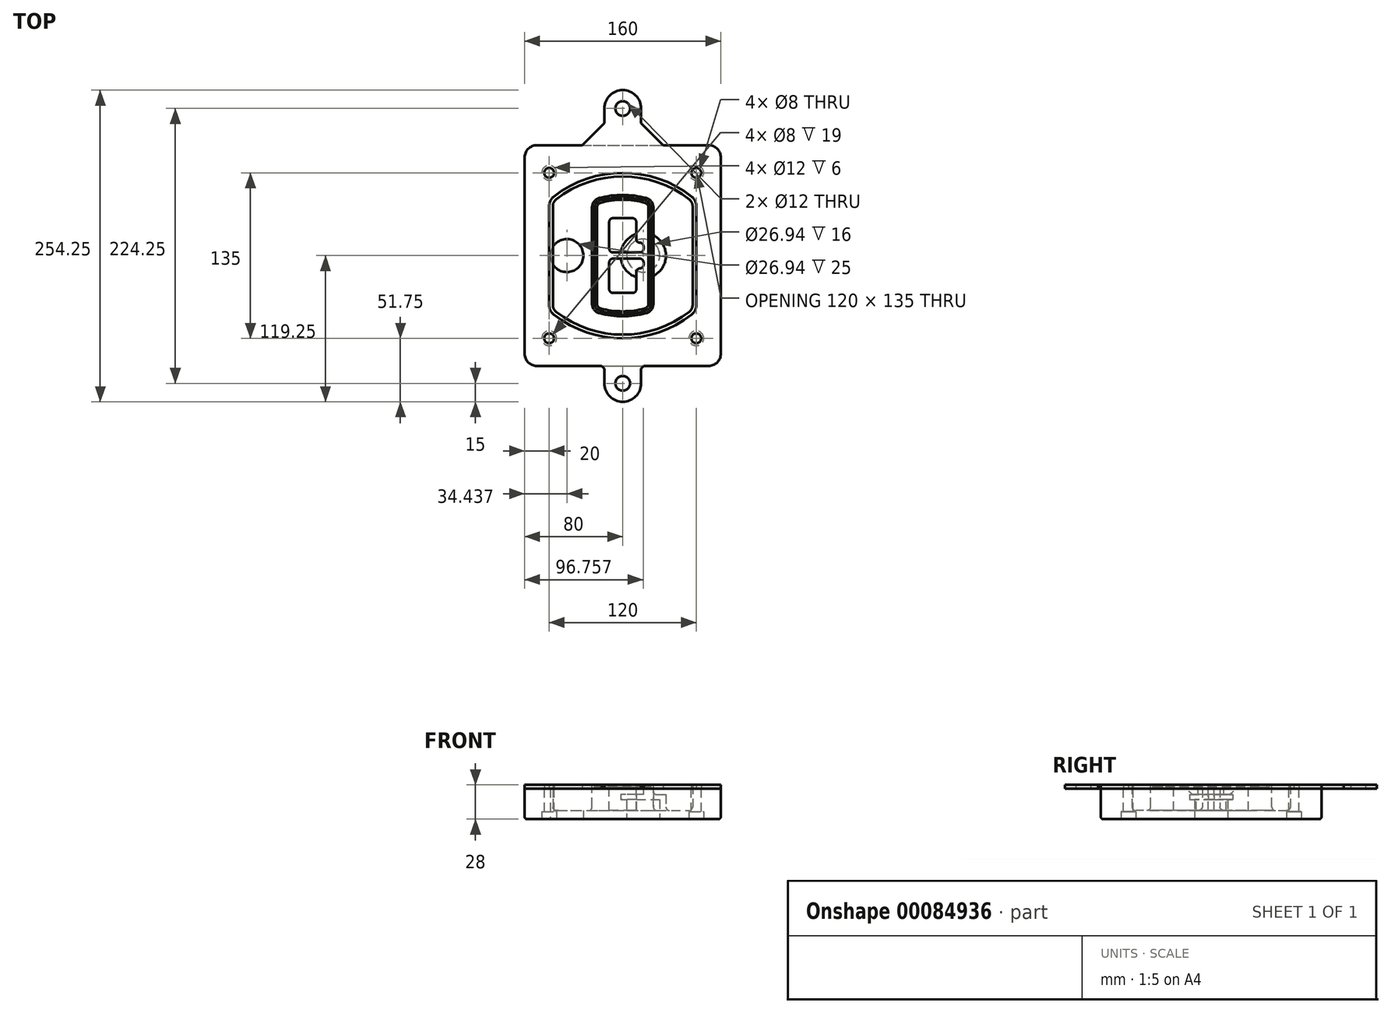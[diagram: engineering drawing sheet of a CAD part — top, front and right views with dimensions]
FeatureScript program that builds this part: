
annotation { "Feature Type Name" : "Feature", "Feature Type Description" : "" }
export const myFeature = defineFeature(function(context is Context, id is Id, definition is map)
    precondition{}
    {
        {
            var Q0;
            Q0=qCreatedBy(makeId("Top.planeOp"),FACE);
            var sketch = newSketch(context, id + "F0", { "sketchPlane" : qUnion([Q0])});
            skPoint(sketch, "E0.rect.middle", {"position": v(0, 0) * mm});
            skLineSegment(sketch, "E1.bottom", {"start": v(-70, -90) * mm, "end": v(70, -90) * mm});
            skLineSegment(sketch, "E1.top", {"start": v(-70, 90) * mm, "end": v(70, 90) * mm});
            skLineSegment(sketch, "E1.left", {"start": v(-80, -80) * mm, "end": v(-80, 80) * mm});
            skLineSegment(sketch, "E1.right", {"start": v(80, -80) * mm, "end": v(80, 80) * mm});
            skLineSegment(sketch, "E2", {"start": v(-80, 90) * mm, "end": v(80, -90) * mm, "construction": true});
            skLineSegment(sketch, "E3", {"start": v(80, 90) * mm, "end": v(-80, -90) * mm, "construction": true});
            skCircle(sketch, "E4", {"center": v(-60, 67.5) * mm, "radius": 4 * mm});
            skCircle(sketch, "E5", {"center": v(60, 67.5) * mm, "radius": 4 * mm});
            skCircle(sketch, "E6", {"center": v(60, -67.5) * mm, "radius": 4 * mm});
            skCircle(sketch, "E7", {"center": v(-60, -67.5) * mm, "radius": 4 * mm});
            skLineSegment(sketch, "E8", {"start": v(-60, 67.5) * mm, "end": v(60, 67.5) * mm, "construction": true});
            skLineSegment(sketch, "E9", {"start": v(60, 67.5) * mm, "end": v(60, -67.5) * mm, "construction": true});
            skLineSegment(sketch, "E10", {"start": v(60, -67.5) * mm, "end": v(-60, -67.5) * mm, "construction": true});
            skLineSegment(sketch, "E11", {"start": v(-60, -67.5) * mm, "end": v(-60, 67.5) * mm, "construction": true});
            skLineSegment(sketch, "E12", {"start": v(-60, 40.3) * mm, "end": v(-60, -40.3) * mm});
            skLineSegment(sketch, "E13", {"start": v(60, 40.3) * mm, "end": v(60, -40.3) * mm});
            skArc(sketch, "E14", {"start": v(56.15, 48.18) * mm, "mid": v(0, 67.5) * mm, "end": v(-56.15, 48.18) * mm});
            skArc(sketch, "E15", {"start": v(-56.15, -48.18) * mm, "mid": v(0, -67.5) * mm, "end": v(56.15, -48.18) * mm});
            skLineSegment(sketch, "E16", {"start": v(-60, 0) * mm, "end": v(60, 0) * mm, "construction": true});
            skPoint(sketch, "E17.visualSharp", {"position": v(-60, -45) * mm});
            skArc(sketch, "E17.filletArc", {"start": v(-60, -40.3) * mm, "mid": v(-58.99, -44.68) * mm, "end": v(-56.15, -48.18) * mm});
            skPoint(sketch, "E18.visualSharp", {"position": v(-60, 45) * mm});
            skArc(sketch, "E18.filletArc", {"start": v(-56.15, 48.18) * mm, "mid": v(-58.99, 44.68) * mm, "end": v(-60, 40.3) * mm});
            skPoint(sketch, "E19.visualSharp", {"position": v(60, 45) * mm});
            skArc(sketch, "E19.filletArc", {"start": v(60, 40.3) * mm, "mid": v(58.99, 44.68) * mm, "end": v(56.15, 48.18) * mm});
            skPoint(sketch, "E20.visualSharp", {"position": v(60, -45) * mm});
            skArc(sketch, "E20.filletArc", {"start": v(56.15, -48.18) * mm, "mid": v(58.99, -44.68) * mm, "end": v(60, -40.3) * mm});
            skPoint(sketch, "E21.visualSharp", {"position": v(-80, 90) * mm});
            skArc(sketch, "E21.filletArc", {"start": v(-70, 90) * mm, "mid": v(-77.07, 87.07) * mm, "end": v(-80, 80) * mm});
            skPoint(sketch, "E22.visualSharp", {"position": v(80, 90) * mm});
            skArc(sketch, "E22.filletArc", {"start": v(80, 80) * mm, "mid": v(77.07, 87.07) * mm, "end": v(70, 90) * mm});
            skPoint(sketch, "E23.visualSharp", {"position": v(80, -90) * mm});
            skArc(sketch, "E23.filletArc", {"start": v(70, -90) * mm, "mid": v(77.07, -87.07) * mm, "end": v(80, -80) * mm});
            skPoint(sketch, "E24.visualSharp", {"position": v(-80, -90) * mm});
            skArc(sketch, "E24.filletArc", {"start": v(-80, -80) * mm, "mid": v(-77.07, -87.07) * mm, "end": v(-70, -90) * mm});
            skArc(sketch, "E25.0", {"start": v(57, 40.3) * mm, "mid": v(56.3, 43.36) * mm, "end": v(54.3, 45.81) * mm});
            skLineSegment(sketch, "E25.1", {"start": v(57, 40.3) * mm, "end": v(57, -40.3) * mm});
            skArc(sketch, "E25.2", {"start": v(54.3, -45.81) * mm, "mid": v(56.3, -43.36) * mm, "end": v(57, -40.3) * mm});
            skArc(sketch, "E25.3", {"start": v(-54.3, -45.81) * mm, "mid": v(0, -64.5) * mm, "end": v(54.3, -45.81) * mm});
            skArc(sketch, "E25.4", {"start": v(-57, -40.3) * mm, "mid": v(-56.3, -43.36) * mm, "end": v(-54.3, -45.81) * mm});
            skArc(sketch, "E25.5", {"start": v(54.3, 45.81) * mm, "mid": v(0, 64.5) * mm, "end": v(-54.3, 45.81) * mm});
            skLineSegment(sketch, "E25.6", {"start": v(-57, 40.3) * mm, "end": v(-57, -40.3) * mm});
            skArc(sketch, "E25.7", {"start": v(-54.3, 45.81) * mm, "mid": v(-56.3, 43.36) * mm, "end": v(-57, 40.3) * mm});
            skArc(sketch, "E26.0", {"start": v(-58.62, 51.33) * mm, "mid": v(-62.58, 46.43) * mm, "end": v(-64, 40.3) * mm});
            skArc(sketch, "E26.1", {"start": v(58.62, 51.33) * mm, "mid": v(0, 71.5) * mm, "end": v(-58.62, 51.33) * mm});
            skArc(sketch, "E26.2", {"start": v(64, 40.3) * mm, "mid": v(62.58, 46.43) * mm, "end": v(58.62, 51.33) * mm});
            skLineSegment(sketch, "E26.3", {"start": v(64, 40.3) * mm, "end": v(64, -40.3) * mm});
            skArc(sketch, "E26.4", {"start": v(58.62, -51.33) * mm, "mid": v(62.58, -46.43) * mm, "end": v(64, -40.3) * mm});
            skLineSegment(sketch, "E26.5", {"start": v(-64, 40.3) * mm, "end": v(-64, -40.3) * mm});
            skArc(sketch, "E26.6", {"start": v(-58.62, -51.33) * mm, "mid": v(0, -71.5) * mm, "end": v(58.62, -51.33) * mm});
            skArc(sketch, "E26.7", {"start": v(-64, -40.3) * mm, "mid": v(-62.58, -46.43) * mm, "end": v(-58.62, -51.33) * mm});
            skSolve(sketch);
        }
        {
            var Q0;
            Q0=makeQuery(id+"F0.imprint","IMPRINT",FACE,{"disambiguationData":[TD([[makeQuery(id+"F0.imprint","IMPRINT",EDGE,{"derivedFrom":sQuery(id+"F0.wireOp",EDGE,"E1.bottom")}),1.0]])]});
            var Q1;
            Q1=makeQuery(id+"F0.imprint","IMPRINT",FACE,{"disambiguationData":[TD([[makeQuery(id+"F0.imprint","IMPRINT",EDGE,{"derivedFrom":sQuery(id+"F0.wireOp",EDGE,"E12")}),1.0]])]});
            var Q2;
            Q2=makeQuery(id+"F0.imprint","IMPRINT",FACE,{"disambiguationData":[TD([[makeQuery(id+"F0.imprint","IMPRINT",EDGE,{"derivedFrom":sQuery(id+"F0.wireOp",EDGE,"E25.0")}),1.0]])]});
            var Q3;
            Q3=makeQuery(id+"F0.imprint","IMPRINT",FACE,{"disambiguationData":[TD([[makeQuery(id+"F0.imprint","IMPRINT",EDGE,{"derivedFrom":sQuery(id+"F0.wireOp",EDGE,"E12")}),-1.0]])]});
            extrude(context, id + "F1", {"entities" : qUnion([Q0, Q1, Q2, Q3]), "oppositeDirection" : true, "depth" : 25 * mm});
        }
        {
            var Q0;
            Q0=makeQuery(id+"F0.imprint","IMPRINT",FACE,{"disambiguationData":[TD([[makeQuery(id+"F0.imprint","IMPRINT",EDGE,{"derivedFrom":sQuery(id+"F0.wireOp",EDGE,"E12")}),1.0]])]});
            extrude(context, id + "F2", {"entities" : qUnion([Q0]), "operationType" : NewBodyOperationType.ADD, "depth" : 3 * mm});
        }
        {
            var Q0;
            Q0=makeQuery(id+"F0.imprint","IMPRINT",FACE,{"disambiguationData":[TD([[makeQuery(id+"F0.imprint","IMPRINT",EDGE,{"derivedFrom":sQuery(id+"F0.wireOp",EDGE,"E25.0")}),1.0]])]});
            extrude(context, id + "F3", {"entities" : qUnion([Q0]), "operationType" : NewBodyOperationType.REMOVE, "oppositeDirection" : true, "depth" : 18 * mm});
        }
        {
            var Q0;
            Q0=makeQuery(id+"F2.opExtrude","CAP_FACE",FACE,{"disambiguationData":[OSD([sQuery(id+"F0.wireOp",EDGE,"E12"),sQuery(id+"F0.wireOp",EDGE,"E13"),sQuery(id+"F0.wireOp",EDGE,"E14"),sQuery(id+"F0.wireOp",EDGE,"E15"),sQuery(id+"F0.wireOp",EDGE,"E17.filletArc"),sQuery(id+"F0.wireOp",EDGE,"E18.filletArc"),sQuery(id+"F0.wireOp",EDGE,"E19.filletArc"),sQuery(id+"F0.wireOp",EDGE,"E20.filletArc"),sQuery(id+"F0.wireOp",EDGE,"E25.0"),sQuery(id+"F0.wireOp",EDGE,"E25.1"),sQuery(id+"F0.wireOp",EDGE,"E25.2"),sQuery(id+"F0.wireOp",EDGE,"E25.3"),sQuery(id+"F0.wireOp",EDGE,"E25.4"),sQuery(id+"F0.wireOp",EDGE,"E25.5"),sQuery(id+"F0.wireOp",EDGE,"E25.6"),sQuery(id+"F0.wireOp",EDGE,"E25.7")])],"isStart":false});
            var sketch = newSketch(context, id + "F4", { "sketchPlane" : qUnion([Q0])});
            skArc(sketch, "E27.0", {"start": v(-19.08, -46.97) * mm, "mid": v(0, -49.5) * mm, "end": v(19.08, -46.97) * mm});
            skArc(sketch, "E28.0", {"start": v(19.08, 46.97) * mm, "mid": v(0, 49.5) * mm, "end": v(-19.08, 46.97) * mm});
            skLineSegment(sketch, "E29", {"start": v(-25, 39.25) * mm, "end": v(-25, -39.25) * mm});
            skLineSegment(sketch, "E30", {"start": v(25, 39.25) * mm, "end": v(25, -39.25) * mm});
            skLineSegment(sketch, "E31", {"start": v(-25, 45.1) * mm, "end": v(25, 45.1) * mm, "construction": true});
            skLineSegment(sketch, "E32", {"start": v(-25, -45.1) * mm, "end": v(25, -45.1) * mm, "construction": true});
            skPoint(sketch, "E33.visualSharp", {"position": v(-25, 45.1) * mm});
            skArc(sketch, "E33.filletArc", {"start": v(-19.08, 46.97) * mm, "mid": v(-23.35, 44.11) * mm, "end": v(-25, 39.25) * mm});
            skPoint(sketch, "E34.visualSharp", {"position": v(25, 45.1) * mm});
            skArc(sketch, "E34.filletArc", {"start": v(25, 39.25) * mm, "mid": v(23.35, 44.11) * mm, "end": v(19.08, 46.97) * mm});
            skPoint(sketch, "E35.visualSharp", {"position": v(25, -45.1) * mm});
            skArc(sketch, "E35.filletArc", {"start": v(19.08, -46.97) * mm, "mid": v(23.35, -44.11) * mm, "end": v(25, -39.25) * mm});
            skPoint(sketch, "E36.visualSharp", {"position": v(-25, -45.1) * mm});
            skArc(sketch, "E36.filletArc", {"start": v(-25, -39.25) * mm, "mid": v(-23.35, -44.11) * mm, "end": v(-19.08, -46.97) * mm});
            skArc(sketch, "E37.0", {"start": v(54.3, 45.81) * mm, "mid": v(0, 64.5) * mm, "end": v(-54.3, 45.81) * mm});
            skArc(sketch, "E37.1", {"start": v(-54.3, 45.81) * mm, "mid": v(-56.3, 43.36) * mm, "end": v(-57, 40.3) * mm});
            skLineSegment(sketch, "E37.2", {"start": v(-57, 40.3) * mm, "end": v(-57, -40.3) * mm});
            skArc(sketch, "E37.3", {"start": v(-57, -40.3) * mm, "mid": v(-56.3, -43.36) * mm, "end": v(-54.3, -45.81) * mm});
            skArc(sketch, "E37.4", {"start": v(-54.3, -45.81) * mm, "mid": v(0, -64.5) * mm, "end": v(54.3, -45.81) * mm});
            skArc(sketch, "E37.5", {"start": v(54.3, -45.81) * mm, "mid": v(56.3, -43.36) * mm, "end": v(57, -40.3) * mm});
            skLineSegment(sketch, "E37.6", {"start": v(57, 40.3) * mm, "end": v(57, -40.3) * mm});
            skArc(sketch, "E37.7", {"start": v(57, 40.3) * mm, "mid": v(56.3, 43.36) * mm, "end": v(54.3, 45.81) * mm});
            skLineSegment(sketch, "E38.0", {"start": v(23, 39.25) * mm, "end": v(23, -39.25) * mm});
            skArc(sketch, "E38.1", {"start": v(18.56, -45.04) * mm, "mid": v(21.76, -42.9) * mm, "end": v(23, -39.25) * mm});
            skArc(sketch, "E38.2", {"start": v(-18.56, -45.04) * mm, "mid": v(0, -47.5) * mm, "end": v(18.56, -45.04) * mm});
            skArc(sketch, "E38.3", {"start": v(-23, -39.25) * mm, "mid": v(-21.76, -42.9) * mm, "end": v(-18.56, -45.04) * mm});
            skLineSegment(sketch, "E38.4", {"start": v(-23, 39.25) * mm, "end": v(-23, -39.25) * mm});
            skArc(sketch, "E38.5", {"start": v(23, 39.25) * mm, "mid": v(21.76, 42.9) * mm, "end": v(18.56, 45.04) * mm});
            skArc(sketch, "E38.6", {"start": v(-18.56, 45.04) * mm, "mid": v(-21.76, 42.9) * mm, "end": v(-23, 39.25) * mm});
            skArc(sketch, "E38.7", {"start": v(18.56, 45.04) * mm, "mid": v(0, 47.5) * mm, "end": v(-18.56, 45.04) * mm});
            skArc(sketch, "E39.0", {"start": v(21, 39.25) * mm, "mid": v(20.18, 41.68) * mm, "end": v(18.04, 43.1) * mm});
            skLineSegment(sketch, "E39.1", {"start": v(21, 39.25) * mm, "end": v(21, -39.25) * mm});
            skArc(sketch, "E39.2", {"start": v(18.04, -43.1) * mm, "mid": v(20.18, -41.68) * mm, "end": v(21, -39.25) * mm});
            skArc(sketch, "E39.3", {"start": v(-18.04, -43.1) * mm, "mid": v(0, -45.5) * mm, "end": v(18.04, -43.1) * mm});
            skArc(sketch, "E39.4", {"start": v(-21, -39.25) * mm, "mid": v(-20.18, -41.68) * mm, "end": v(-18.04, -43.1) * mm});
            skArc(sketch, "E39.5", {"start": v(18.04, 43.1) * mm, "mid": v(0, 45.5) * mm, "end": v(-18.04, 43.1) * mm});
            skLineSegment(sketch, "E39.6", {"start": v(-21, 39.25) * mm, "end": v(-21, -39.25) * mm});
            skArc(sketch, "E39.7", {"start": v(-18.04, 43.1) * mm, "mid": v(-20.18, 41.68) * mm, "end": v(-21, 39.25) * mm});
            skLineSegment(sketch, "E40", {"start": v(-25, 0) * mm, "end": v(25, 0) * mm, "construction": true});
            skLineSegment(sketch, "E41", {"start": v(-11, 5.5) * mm, "end": v(-11, 27.5) * mm});
            skLineSegment(sketch, "E42", {"start": v(-8, 30.5) * mm, "end": v(8, 30.5) * mm});
            skLineSegment(sketch, "E43", {"start": v(11, 27.5) * mm, "end": v(11, 13.5) * mm});
            skLineSegment(sketch, "E44", {"start": v(14, 10.5) * mm, "end": v(14, 10.5) * mm});
            skLineSegment(sketch, "E45", {"start": v(17, 7.5) * mm, "end": v(17, 5.5) * mm});
            skLineSegment(sketch, "E46", {"start": v(14, 2.5) * mm, "end": v(-8, 2.5) * mm});
            skPoint(sketch, "E47.visualSharp", {"position": v(-11, 30.5) * mm});
            skArc(sketch, "E47.filletArc", {"start": v(-8, 30.5) * mm, "mid": v(-10.12, 29.62) * mm, "end": v(-11, 27.5) * mm});
            skPoint(sketch, "E48.visualSharp", {"position": v(11, 30.5) * mm});
            skArc(sketch, "E48.filletArc", {"start": v(11, 27.5) * mm, "mid": v(10.12, 29.62) * mm, "end": v(8, 30.5) * mm});
            skPoint(sketch, "E49.visualSharp", {"position": v(11, 10.5) * mm});
            skArc(sketch, "E49.filletArc", {"start": v(11, 13.5) * mm, "mid": v(11.88, 11.38) * mm, "end": v(14, 10.5) * mm});
            skPoint(sketch, "E50.visualSharp", {"position": v(17, 10.5) * mm});
            skArc(sketch, "E50.filletArc", {"start": v(17, 7.5) * mm, "mid": v(16.12, 9.62) * mm, "end": v(14, 10.5) * mm});
            skPoint(sketch, "E51.visualSharp", {"position": v(17, 2.5) * mm});
            skArc(sketch, "E51.filletArc", {"start": v(14, 2.5) * mm, "mid": v(16.12, 3.38) * mm, "end": v(17, 5.5) * mm});
            skPoint(sketch, "E52.visualSharp", {"position": v(-11, 2.5) * mm});
            skArc(sketch, "E52.filletArc", {"start": v(-11, 5.5) * mm, "mid": v(-10.12, 3.38) * mm, "end": v(-8, 2.5) * mm});
            skLineSegment(sketch, "E53.0.MirrorCS", {"start": v(14, -2.5) * mm, "end": v(-8, -2.5) * mm});
            skArc(sketch, "E54.0.MirrorCS", {"start": v(-11, -5.5) * mm, "mid": v(-10.12, -3.38) * mm, "end": v(-8, -2.5) * mm});
            skLineSegment(sketch, "E55.0.MirrorCS", {"start": v(-11, -5.5) * mm, "end": v(-11, -27.5) * mm});
            skArc(sketch, "E56.0.MirrorCS", {"start": v(-8, -30.5) * mm, "mid": v(-10.12, -29.62) * mm, "end": v(-11, -27.5) * mm});
            skLineSegment(sketch, "E57.0.MirrorCS", {"start": v(-8, -30.5) * mm, "end": v(8, -30.5) * mm});
            skArc(sketch, "E58.0.MirrorCS", {"start": v(11, -27.5) * mm, "mid": v(10.12, -29.62) * mm, "end": v(8, -30.5) * mm});
            skLineSegment(sketch, "E59.0.MirrorCS", {"start": v(11, -27.5) * mm, "end": v(11, -13.5) * mm});
            skArc(sketch, "E60.0.MirrorCS", {"start": v(11, -13.5) * mm, "mid": v(11.88, -11.38) * mm, "end": v(14, -10.5) * mm});
            skArc(sketch, "E61.0.MirrorCS", {"start": v(17, -7.5) * mm, "mid": v(16.12, -9.62) * mm, "end": v(14, -10.5) * mm});
            skLineSegment(sketch, "E62.0.MirrorCS", {"start": v(17, -7.5) * mm, "end": v(17, -5.5) * mm});
            skArc(sketch, "E63.0.MirrorCS", {"start": v(14, -2.5) * mm, "mid": v(16.12, -3.38) * mm, "end": v(17, -5.5) * mm});
            skSolve(sketch);
        }
        {
            var Q0;
            Q0=makeQuery(id+"F4.imprint","IMPRINT",FACE,{"disambiguationData":[TD([[makeQuery(id+"F4.imprint","IMPRINT",EDGE,{"derivedFrom":sQuery(id+"F4.wireOp",EDGE,"E27.0")}),1.0]])]});
            var Q1;
            Q1=makeQuery(id+"F4.imprint","IMPRINT",FACE,{"disambiguationData":[TD([[makeQuery(id+"F4.imprint","IMPRINT",EDGE,{"derivedFrom":sQuery(id+"F4.wireOp",EDGE,"E38.0")}),-1.0]])]});
            var Q2;
            Q2=makeQuery(id+"F4.imprint","IMPRINT",FACE,{"disambiguationData":[TD([[makeQuery(id+"F4.imprint","IMPRINT",EDGE,{"derivedFrom":sQuery(id+"F4.wireOp",EDGE,"E39.0")}),1.0]])]});
            extrude(context, id + "F5", {"entities" : qUnion([Q0, Q1, Q2]), "operationType" : NewBodyOperationType.ADD, "endBound" : BoundingType.UP_TO_NEXT, "oppositeDirection" : true, "depth" : 25 * mm});
        }
        {
            var Q0;
            Q0=makeQuery(id+"F4.imprint","IMPRINT",FACE,{"disambiguationData":[TD([[makeQuery(id+"F4.imprint","IMPRINT",EDGE,{"derivedFrom":sQuery(id+"F4.wireOp",EDGE,"E38.0")}),-1.0]])]});
            extrude(context, id + "F6", {"entities" : qUnion([Q0]), "operationType" : NewBodyOperationType.REMOVE, "oppositeDirection" : true, "depth" : 2 * mm});
        }
        {
            var Q0;
            Q0=makeQuery(id+"F1.opExtrude","CAP_FACE",FACE,{"disambiguationData":[OSD([sQuery(id+"F0.wireOp",EDGE,"E1.bottom"),sQuery(id+"F0.wireOp",EDGE,"E1.top"),sQuery(id+"F0.wireOp",EDGE,"E1.left"),sQuery(id+"F0.wireOp",EDGE,"E1.right"),sQuery(id+"F0.wireOp",EDGE,"E4"),sQuery(id+"F0.wireOp",EDGE,"E5"),sQuery(id+"F0.wireOp",EDGE,"E6"),sQuery(id+"F0.wireOp",EDGE,"E7"),sQuery(id+"F0.wireOp",EDGE,"E21.filletArc"),sQuery(id+"F0.wireOp",EDGE,"E22.filletArc"),sQuery(id+"F0.wireOp",EDGE,"E23.filletArc"),sQuery(id+"F0.wireOp",EDGE,"E24.filletArc")])],"isStart":false});
            var sketch = newSketch(context, id + "F7", { "sketchPlane" : qUnion([Q0])});
            skCircle(sketch, "E64", {"center": v(16.76, 0) * mm, "radius": 13.47 * mm});
            skCircle(sketch, "E65", {"center": v(-45.56, 0) * mm, "radius": 13.47 * mm});
            skLineSegment(sketch, "E66", {"start": v(80, 0) * mm, "end": v(-80, 0) * mm});
            skCircle(sketch, "E67", {"center": v(16.76, 0) * mm, "radius": 18.47 * mm});
            skCircle(sketch, "E68", {"center": v(60, -67.5) * mm, "radius": 6 * mm});
            skCircle(sketch, "E69", {"center": v(-60, -67.5) * mm, "radius": 6 * mm});
            skCircle(sketch, "E70", {"center": v(-60, 67.5) * mm, "radius": 6 * mm});
            skCircle(sketch, "E71", {"center": v(60, 67.5) * mm, "radius": 6 * mm});
            skSolve(sketch);
        }
        {
            var Q0;
            {var subQ1=sQuery(id+"F7.wireOp",EDGE,"E66");var subQ4=sQuery(id+"F7.wireOp",EDGE,"E64");var subQ6=makeQuery(id+"F7.imprint","INTERSECT",VERTEX,{"disambiguationData":[OD(0.0)],"derivedFrom":[subQ4,subQ1]});Q0=makeQuery(id+"F7.imprint","IMPRINT",FACE,{"disambiguationData":[TD([[makeQuery(id+"F7.imprint","IMPRINT",EDGE,{"disambiguationData":[TD([[subQ6,-1.0]])],"derivedFrom":subQ4}),-1.0]])]});}
            var Q1;
            {var subQ0=sQuery(id+"F7.wireOp",EDGE,"E66");var subQ1=sQuery(id+"F7.wireOp",EDGE,"E64");var subQ3=makeQuery(id+"F7.imprint","INTERSECT",VERTEX,{"disambiguationData":[OD(0.0)],"derivedFrom":[subQ1,subQ0]});Q1=makeQuery(id+"F7.imprint","IMPRINT",FACE,{"disambiguationData":[TD([[makeQuery(id+"F7.imprint","IMPRINT",EDGE,{"disambiguationData":[TD([[subQ3,-1.0]])],"derivedFrom":subQ1}),1.0]])]});}
            var Q2;
            {var subQ0=sQuery(id+"F7.wireOp",EDGE,"E66");var subQ1=sQuery(id+"F7.wireOp",EDGE,"E64");var subQ3=makeQuery(id+"F7.imprint","INTERSECT",VERTEX,{"disambiguationData":[OD(0.0)],"derivedFrom":[subQ1,subQ0]});Q2=makeQuery(id+"F7.imprint","IMPRINT",FACE,{"disambiguationData":[TD([[makeQuery(id+"F7.imprint","IMPRINT",EDGE,{"disambiguationData":[TD([[subQ3,1.0]])],"derivedFrom":subQ1}),1.0]])]});}
            var Q3;
            {var subQ1=sQuery(id+"F7.wireOp",EDGE,"E66");var subQ4=sQuery(id+"F7.wireOp",EDGE,"E64");var subQ6=makeQuery(id+"F7.imprint","INTERSECT",VERTEX,{"disambiguationData":[OD(0.0)],"derivedFrom":[subQ4,subQ1]});Q3=makeQuery(id+"F7.imprint","IMPRINT",FACE,{"disambiguationData":[TD([[makeQuery(id+"F7.imprint","IMPRINT",EDGE,{"disambiguationData":[TD([[subQ6,1.0]])],"derivedFrom":subQ4}),-1.0]])]});}
            extrude(context, id + "F8", {"entities" : qUnion([Q0, Q1, Q2, Q3]), "operationType" : NewBodyOperationType.ADD, "oppositeDirection" : true, "depth" : 20 * mm});
        }
        {
            var Q0;
            {var subQ0=sQuery(id+"F7.wireOp",EDGE,"E66");var subQ1=sQuery(id+"F7.wireOp",EDGE,"E64");var subQ3=makeQuery(id+"F7.imprint","INTERSECT",VERTEX,{"disambiguationData":[OD(0.0)],"derivedFrom":[subQ1,subQ0]});Q0=makeQuery(id+"F7.imprint","IMPRINT",FACE,{"disambiguationData":[TD([[makeQuery(id+"F7.imprint","IMPRINT",EDGE,{"disambiguationData":[TD([[subQ3,-1.0]])],"derivedFrom":subQ1}),1.0]])]});}
            var Q1;
            {var subQ0=sQuery(id+"F7.wireOp",EDGE,"E66");var subQ1=sQuery(id+"F7.wireOp",EDGE,"E64");var subQ3=makeQuery(id+"F7.imprint","INTERSECT",VERTEX,{"disambiguationData":[OD(0.0)],"derivedFrom":[subQ1,subQ0]});Q1=makeQuery(id+"F7.imprint","IMPRINT",FACE,{"disambiguationData":[TD([[makeQuery(id+"F7.imprint","IMPRINT",EDGE,{"disambiguationData":[TD([[subQ3,1.0]])],"derivedFrom":subQ1}),1.0]])]});}
            extrude(context, id + "F9", {"entities" : qUnion([Q0, Q1]), "operationType" : NewBodyOperationType.REMOVE, "oppositeDirection" : true, "depth" : 16 * mm});
        }
        {
            var Q0;
            {var subQ0=sQuery(id+"F7.wireOp",EDGE,"E66");var subQ1=sQuery(id+"F7.wireOp",EDGE,"E65");var subQ3=makeQuery(id+"F7.imprint","INTERSECT",VERTEX,{"disambiguationData":[OD(0.0)],"derivedFrom":[subQ1,subQ0]});Q0=makeQuery(id+"F7.imprint","IMPRINT",FACE,{"disambiguationData":[TD([[makeQuery(id+"F7.imprint","IMPRINT",EDGE,{"disambiguationData":[TD([[subQ3,-1.0]])],"derivedFrom":subQ1}),1.0]])]});}
            var Q1;
            {var subQ0=sQuery(id+"F7.wireOp",EDGE,"E66");var subQ1=sQuery(id+"F7.wireOp",EDGE,"E65");var subQ3=makeQuery(id+"F7.imprint","INTERSECT",VERTEX,{"disambiguationData":[OD(0.0)],"derivedFrom":[subQ1,subQ0]});Q1=makeQuery(id+"F7.imprint","IMPRINT",FACE,{"disambiguationData":[TD([[makeQuery(id+"F7.imprint","IMPRINT",EDGE,{"disambiguationData":[TD([[subQ3,1.0]])],"derivedFrom":subQ1}),1.0]])]});}
            extrude(context, id + "F10", {"entities" : qUnion([Q0, Q1]), "operationType" : NewBodyOperationType.REMOVE, "oppositeDirection" : true, "depth" : 25 * mm});
        }
        {
            var Q0;
            Q0=makeQuery(id+"F7.imprint","IMPRINT",FACE,{"disambiguationData":[TD([[makeQuery(id+"F7.imprint","IMPRINT",EDGE,{"derivedFrom":sQuery(id+"F7.wireOp",EDGE,"E68")}),1.0]])]});
            var Q1;
            Q1=makeQuery(id+"F7.imprint","IMPRINT",FACE,{"disambiguationData":[TD([[makeQuery(id+"F7.imprint","IMPRINT",EDGE,{"derivedFrom":makeQuery(id+"F1.opExtrude","CAP_EDGE",EDGE,{"disambiguationData":[OSD([sQuery(id+"F0.wireOp",EDGE,"E5")])],"isStart":false})}),-1.0]])]});
            var Q2;
            Q2=makeQuery(id+"F7.imprint","IMPRINT",FACE,{"disambiguationData":[TD([[makeQuery(id+"F7.imprint","IMPRINT",EDGE,{"derivedFrom":sQuery(id+"F7.wireOp",EDGE,"E69")}),1.0]])]});
            var Q3;
            Q3=makeQuery(id+"F7.imprint","IMPRINT",FACE,{"disambiguationData":[TD([[makeQuery(id+"F7.imprint","IMPRINT",EDGE,{"derivedFrom":makeQuery(id+"F1.opExtrude","CAP_EDGE",EDGE,{"disambiguationData":[OSD([sQuery(id+"F0.wireOp",EDGE,"E4")])],"isStart":false})}),-1.0]])]});
            var Q4;
            Q4=makeQuery(id+"F7.imprint","IMPRINT",FACE,{"disambiguationData":[TD([[makeQuery(id+"F7.imprint","IMPRINT",EDGE,{"derivedFrom":sQuery(id+"F7.wireOp",EDGE,"E70")}),1.0]])]});
            var Q5;
            Q5=makeQuery(id+"F7.imprint","IMPRINT",FACE,{"disambiguationData":[TD([[makeQuery(id+"F7.imprint","IMPRINT",EDGE,{"derivedFrom":makeQuery(id+"F1.opExtrude","CAP_EDGE",EDGE,{"disambiguationData":[OSD([sQuery(id+"F0.wireOp",EDGE,"E7")])],"isStart":false})}),-1.0]])]});
            var Q6;
            Q6=makeQuery(id+"F7.imprint","IMPRINT",FACE,{"disambiguationData":[TD([[makeQuery(id+"F7.imprint","IMPRINT",EDGE,{"derivedFrom":sQuery(id+"F7.wireOp",EDGE,"E71")}),1.0]])]});
            var Q7;
            Q7=makeQuery(id+"F7.imprint","IMPRINT",FACE,{"disambiguationData":[TD([[makeQuery(id+"F7.imprint","IMPRINT",EDGE,{"derivedFrom":makeQuery(id+"F1.opExtrude","CAP_EDGE",EDGE,{"disambiguationData":[OSD([sQuery(id+"F0.wireOp",EDGE,"E6")])],"isStart":false})}),-1.0]])]});
            extrude(context, id + "F11", {"entities" : qUnion([Q0, Q1, Q2, Q3, Q4, Q5, Q6, Q7]), "operationType" : NewBodyOperationType.REMOVE, "oppositeDirection" : true, "depth" : 6 * mm});
        }
        {
            var Q0;
            Q0=makeQuery(id+"F9.boolean.opBoolean","COPY",FACE,{"derivedFrom":makeQuery(id+"F9.opExtrude","CAP_FACE",FACE,{"disambiguationData":[OSD([sQuery(id+"F7.wireOp",EDGE,"E64")])],"isStart":false})});
            var sketch = newSketch(context, id + "F12", { "sketchPlane" : qUnion([Q0])});
            skArc(sketch, "E72.0", {"start": v(11, 17.55) * mm, "mid": v(2.57, 11.82) * mm, "end": v(-1.54, 2.5) * mm});
            skArc(sketch, "E72.1", {"start": v(-1.54, -2.5) * mm, "mid": v(2.57, -11.82) * mm, "end": v(11, -17.55) * mm});
            skLineSegment(sketch, "E73", {"start": v(-1.54, -2.5) * mm, "end": v(14, -2.5) * mm});
            skLineSegment(sketch, "E74.0", {"start": v(14, 2.5) * mm, "end": v(-1.54, 2.5) * mm});
            skArc(sketch, "E74.1", {"start": v(14, 2.5) * mm, "mid": v(16.12, 3.38) * mm, "end": v(17, 5.5) * mm});
            skLineSegment(sketch, "E74.2", {"start": v(17, 7.5) * mm, "end": v(17, 5.5) * mm});
            skArc(sketch, "E74.3", {"start": v(17, 7.5) * mm, "mid": v(16.12, 9.62) * mm, "end": v(14, 10.5) * mm});
            skArc(sketch, "E74.4", {"start": v(11, 13.5) * mm, "mid": v(11.88, 11.38) * mm, "end": v(14, 10.5) * mm});
            skLineSegment(sketch, "E74.5", {"start": v(11, 17.55) * mm, "end": v(11, 13.5) * mm});
            skLineSegment(sketch, "E74.7", {"start": v(14, -2.5) * mm, "end": v(-1.54, -2.5) * mm});
            skArc(sketch, "E74.8", {"start": v(14, -2.5) * mm, "mid": v(16.12, -3.38) * mm, "end": v(17, -5.5) * mm});
            skLineSegment(sketch, "E74.9", {"start": v(17, -7.5) * mm, "end": v(17, -5.5) * mm});
            skArc(sketch, "E74.10", {"start": v(17, -7.5) * mm, "mid": v(16.12, -9.62) * mm, "end": v(14, -10.5) * mm});
            skArc(sketch, "E74.11", {"start": v(11, -13.5) * mm, "mid": v(11.88, -11.38) * mm, "end": v(14, -10.5) * mm});
            skLineSegment(sketch, "E74.12", {"start": v(11, -17.55) * mm, "end": v(11, -13.5) * mm});
            skPoint(sketch, "E75.orphan", {"position": v(11, -27.5) * mm});
            skPoint(sketch, "E76.orphan", {"position": v(-8, -2.5) * mm});
            skPoint(sketch, "E77.orphan", {"position": v(-8, 2.5) * mm});
            skPoint(sketch, "E78.orphan", {"position": v(11, 27.5) * mm});
            skSolve(sketch);
        }
        {
            var Q0;
            {var subQ7=sQuery(id+"F12.wireOp",EDGE,"E72.0");var subQ14=sQuery(id+"F12.wireOp",EDGE,"E72.1");var subQ16=sQuery(id+"F12.wireOp",EDGE,"E74.1");var subQ18=sQuery(id+"F12.wireOp",EDGE,"E74.8");Q0=qUnion([makeQuery(id+"F12.imprint","IMPRINT",FACE,{"disambiguationData":[TD([[makeQuery(id+"F12.imprint","IMPRINT",EDGE,{"derivedFrom":subQ7}),1.0]])]}),makeQuery(id+"F12.imprint","IMPRINT",FACE,{"disambiguationData":[TD([[makeQuery(id+"F12.imprint","IMPRINT",EDGE,{"derivedFrom":subQ14}),1.0]])]}),makeQuery(id+"F12.imprint","IMPRINT",FACE,{"disambiguationData":[TD([[makeQuery(id+"F12.imprint","IMPRINT",EDGE,{"derivedFrom":subQ16}),1.0]])]}),makeQuery(id+"F12.imprint","IMPRINT",FACE,{"disambiguationData":[TD([[makeQuery(id+"F12.imprint","IMPRINT",EDGE,{"derivedFrom":subQ18}),-1.0]])]})]);}
            var Q1;
            Q1=makeQuery(id+"F5.boolean.opBoolean","SPLIT",FACE,{"disambiguationData":[TD([makeQuery(id+"F5.opExtrude","SWEPT_FACE",FACE,{"disambiguationData":[OSD([sQuery(id+"F4.wireOp",EDGE,"E41")])]})])],"derivedFrom":makeQuery(id+"F3.boolean.opBoolean","COPY",FACE,{"derivedFrom":makeQuery(id+"F3.opExtrude","CAP_FACE",FACE,{"disambiguationData":[OSD([sQuery(id+"F0.wireOp",EDGE,"E25.0"),sQuery(id+"F0.wireOp",EDGE,"E25.1"),sQuery(id+"F0.wireOp",EDGE,"E25.2"),sQuery(id+"F0.wireOp",EDGE,"E25.3"),sQuery(id+"F0.wireOp",EDGE,"E25.4"),sQuery(id+"F0.wireOp",EDGE,"E25.5"),sQuery(id+"F0.wireOp",EDGE,"E25.6"),sQuery(id+"F0.wireOp",EDGE,"E25.7")])],"isStart":false})})});
            extrude(context, id + "F13", {"entities" : qUnion([Q0]), "operationType" : NewBodyOperationType.REMOVE, "endBound" : BoundingType.UP_TO_SURFACE, "endBoundEntityFace" : qUnion([Q1]), "depth" : 25 * mm});
        }
        {
            var Q0;
            Q0=makeQuery(id+"F3.boolean.opBoolean","COPY",EDGE,{"derivedFrom":makeQuery(id+"F3.opExtrude","CAP_EDGE",EDGE,{"disambiguationData":[OSD([sQuery(id+"F0.wireOp",EDGE,"E25.6")])],"isStart":false})});
            var Q1;
            Q1=makeQuery(id+"F8.boolean.opBoolean","INTERSECT",EDGE,{"derivedFrom":[makeQuery(id+"F5.opExtrude","SWEPT_FACE",FACE,{"disambiguationData":[OSD([sQuery(id+"F4.wireOp",EDGE,"E30")])]}),makeQuery(id+"F8.opExtrude","CAP_FACE",FACE,{"disambiguationData":[OSD([sQuery(id+"F7.wireOp",EDGE,"E67")])],"isStart":false})]});
            var Q2;
            Q2=makeQuery(id+"F8.boolean.opBoolean","INTERSECT",EDGE,{"disambiguationData":[OD(1.0)],"derivedFrom":[makeQuery(id+"F5.opExtrude","SWEPT_FACE",FACE,{"disambiguationData":[OSD([sQuery(id+"F4.wireOp",EDGE,"E30")])]}),makeQuery(id+"F8.opExtrude","SWEPT_FACE",FACE,{"disambiguationData":[OSD([sQuery(id+"F7.wireOp",EDGE,"E67")])]})]});
            var Q3;
            {var subQ0=sQuery(id+"F4.wireOp",EDGE,"E30");Q3=makeQuery(id+"F8.boolean.opBoolean","SPLIT",EDGE,{"disambiguationData":[TD([makeQuery(id+"F5.opExtrude","SWEPT_FACE",FACE,{"disambiguationData":[OSD([sQuery(id+"F4.wireOp",EDGE,"E35.filletArc")])]})])],"derivedFrom":makeQuery(id+"F5.opExtrude","CAP_EDGE",EDGE,{"disambiguationData":[OSD([subQ0])],"isStart":false})});}
            var Q4;
            {var subQ0=sQuery(id+"F0.wireOp",EDGE,"E25.7");var subQ1=sQuery(id+"F0.wireOp",EDGE,"E25.1");var subQ2=sQuery(id+"F0.wireOp",EDGE,"E25.6");var subQ3=sQuery(id+"F0.wireOp",EDGE,"E25.5");var subQ4=sQuery(id+"F0.wireOp",EDGE,"E25.4");var subQ5=sQuery(id+"F0.wireOp",EDGE,"E25.0");var subQ6=sQuery(id+"F0.wireOp",EDGE,"E25.2");var subQ7=sQuery(id+"F0.wireOp",EDGE,"E25.3");Q4=makeQuery(id+"F8.boolean.opBoolean","INTERSECT",EDGE,{"derivedFrom":[makeQuery(id+"F5.boolean.opBoolean","SPLIT",FACE,{"disambiguationData":[TD([makeQuery(id+"F2.opExtrude","SWEPT_FACE",FACE,{"disambiguationData":[OSD([subQ5])]})])],"derivedFrom":makeQuery(id+"F3.boolean.opBoolean","COPY",FACE,{"derivedFrom":makeQuery(id+"F3.opExtrude","CAP_FACE",FACE,{"disambiguationData":[OSD([subQ5,subQ1,subQ6,subQ7,subQ4,subQ3,subQ2,subQ0])],"isStart":false})})}),makeQuery(id+"F8.opExtrude","SWEPT_FACE",FACE,{"disambiguationData":[OSD([sQuery(id+"F7.wireOp",EDGE,"E67")])]})]});}
            var Q5;
            Q5=makeQuery(id+"F8.boolean.opBoolean","INTERSECT",EDGE,{"disambiguationData":[OD(0.0)],"derivedFrom":[makeQuery(id+"F5.opExtrude","SWEPT_FACE",FACE,{"disambiguationData":[OSD([sQuery(id+"F4.wireOp",EDGE,"E30")])]}),makeQuery(id+"F8.opExtrude","SWEPT_FACE",FACE,{"disambiguationData":[OSD([sQuery(id+"F7.wireOp",EDGE,"E67")])]})]});
            fillet(context, id + "F14", {"entities" : qUnion([Q0, Q1, Q2, Q3, Q4, Q5]), "radius" : 3 * mm, "tangentPropagation" : true, "allowEdgeOverflow" : false});
        }
        {
            var Q0;
            Q0=makeQuery(id+"F1.opExtrude","CAP_EDGE",EDGE,{"disambiguationData":[OSD([sQuery(id+"F0.wireOp",EDGE,"E1.bottom")])],"isStart":false});
            fillet(context, id + "F15", {"entities" : qUnion([Q0]), "radius" : 2 * mm, "tangentPropagation" : true, "allowEdgeOverflow" : false});
        }
        {
            var Q0;
            {var subQ0=sQuery(id+"F0.wireOp",EDGE,"E22.filletArc");var subQ1=sQuery(id+"F0.wireOp",EDGE,"E7");var subQ2=sQuery(id+"F0.wireOp",EDGE,"E6");var subQ3=sQuery(id+"F0.wireOp",EDGE,"E5");var subQ4=sQuery(id+"F0.wireOp",EDGE,"E4");var subQ5=sQuery(id+"F0.wireOp",EDGE,"E1.bottom");var subQ6=sQuery(id+"F0.wireOp",EDGE,"E21.filletArc");var subQ7=sQuery(id+"F0.wireOp",EDGE,"E1.top");var subQ8=sQuery(id+"F0.wireOp",EDGE,"E1.left");var subQ9=sQuery(id+"F0.wireOp",EDGE,"E1.right");var subQ10=sQuery(id+"F0.wireOp",EDGE,"E23.filletArc");var subQ11=sQuery(id+"F0.wireOp",EDGE,"E24.filletArc");Q0=makeQuery(id+"F2.boolean.opBoolean","SPLIT",FACE,{"disambiguationData":[TD([makeQuery(id+"F1.opExtrude","SWEPT_FACE",FACE,{"disambiguationData":[OSD([subQ5])]})])],"derivedFrom":makeQuery(id+"F1.opExtrude","CAP_FACE",FACE,{"disambiguationData":[OSD([subQ5,subQ7,subQ8,subQ9,subQ4,subQ3,subQ2,subQ1,subQ6,subQ0,subQ10,subQ11])],"isStart":true})});}
            var sketch = newSketch(context, id + "F16", { "sketchPlane" : qUnion([Q0])});
            skLineSegment(sketch, "E79", {"start": v(-33, 90) * mm, "end": v(-15, 108) * mm});
            skLineSegment(sketch, "E80", {"start": v(33, 90) * mm, "end": v(15, 108) * mm});
            skLineSegment(sketch, "E81", {"start": v(15, 108) * mm, "end": v(15, 120) * mm});
            skLineSegment(sketch, "E82", {"start": v(-15, 108) * mm, "end": v(-15, 120) * mm});
            skArc(sketch, "E83", {"start": v(15, 120) * mm, "mid": v(0, 135) * mm, "end": v(-15, 120) * mm});
            skCircle(sketch, "E84", {"center": v(0, 120) * mm, "radius": 6 * mm});
            skLineSegment(sketch, "E85.MirrorCS", {"start": v(-33, -74.25) * mm, "end": v(-15, -92.25) * mm});
            skLineSegment(sketch, "E86.MirrorCS", {"start": v(-15, -92.25) * mm, "end": v(-15, -104.25) * mm});
            skArc(sketch, "E87.MirrorCS", {"start": v(15, -104.25) * mm, "mid": v(0, -119.25) * mm, "end": v(-15, -104.25) * mm});
            skLineSegment(sketch, "E88.MirrorCS", {"start": v(15, -92.25) * mm, "end": v(15, -104.25) * mm});
            skLineSegment(sketch, "E89.MirrorCS", {"start": v(33, -74.25) * mm, "end": v(15, -92.25) * mm});
            skCircle(sketch, "E90.MirrorC", {"center": v(0, -104.25) * mm, "radius": 6 * mm});
            skSolve(sketch);
        }
        {
            var Q0;
            Q0=makeQuery(id+"F16.imprint","IMPRINT",FACE,{"disambiguationData":[TD([[makeQuery(id+"F16.imprint","IMPRINT",EDGE,{"derivedFrom":makeQuery(id+"F1.opExtrude","CAP_EDGE",EDGE,{"disambiguationData":[OSD([sQuery(id+"F0.wireOp",EDGE,"E1.left")])],"isStart":true})}),-1.0]])]});
            var Q1;
            {var subQ0=sQuery(id+"F16.wireOp",EDGE,"E85.MirrorCS");Q1=makeQuery(id+"F16.imprint","IMPRINT",FACE,{"disambiguationData":[TD([[makeQuery(id+"F16.imprint","IMPRINT",EDGE,{"derivedFrom":subQ0}),1.0]])]});}
            var Q2;
            {var subQ0=sQuery(id+"F16.wireOp",EDGE,"E79");Q2=makeQuery(id+"F16.imprint","IMPRINT",FACE,{"disambiguationData":[TD([[makeQuery(id+"F16.imprint","IMPRINT",EDGE,{"derivedFrom":subQ0}),-1.0]])]});}
            var Q3;
            Q3=makeQuery(id+"F2.opExtrude","CAP_FACE",FACE,{"disambiguationData":[OSD([sQuery(id+"F0.wireOp",EDGE,"E12"),sQuery(id+"F0.wireOp",EDGE,"E13"),sQuery(id+"F0.wireOp",EDGE,"E14"),sQuery(id+"F0.wireOp",EDGE,"E15"),sQuery(id+"F0.wireOp",EDGE,"E17.filletArc"),sQuery(id+"F0.wireOp",EDGE,"E18.filletArc"),sQuery(id+"F0.wireOp",EDGE,"E19.filletArc"),sQuery(id+"F0.wireOp",EDGE,"E20.filletArc"),sQuery(id+"F0.wireOp",EDGE,"E25.0"),sQuery(id+"F0.wireOp",EDGE,"E25.1"),sQuery(id+"F0.wireOp",EDGE,"E25.2"),sQuery(id+"F0.wireOp",EDGE,"E25.3"),sQuery(id+"F0.wireOp",EDGE,"E25.4"),sQuery(id+"F0.wireOp",EDGE,"E25.5"),sQuery(id+"F0.wireOp",EDGE,"E25.6"),sQuery(id+"F0.wireOp",EDGE,"E25.7")])],"isStart":false});
            extrude(context, id + "F17", {"entities" : qUnion([Q0, Q1, Q2]), "endBound" : BoundingType.UP_TO_SURFACE, "endBoundEntityFace" : qUnion([Q3]), "depth" : 25 * mm});
        }
    });
